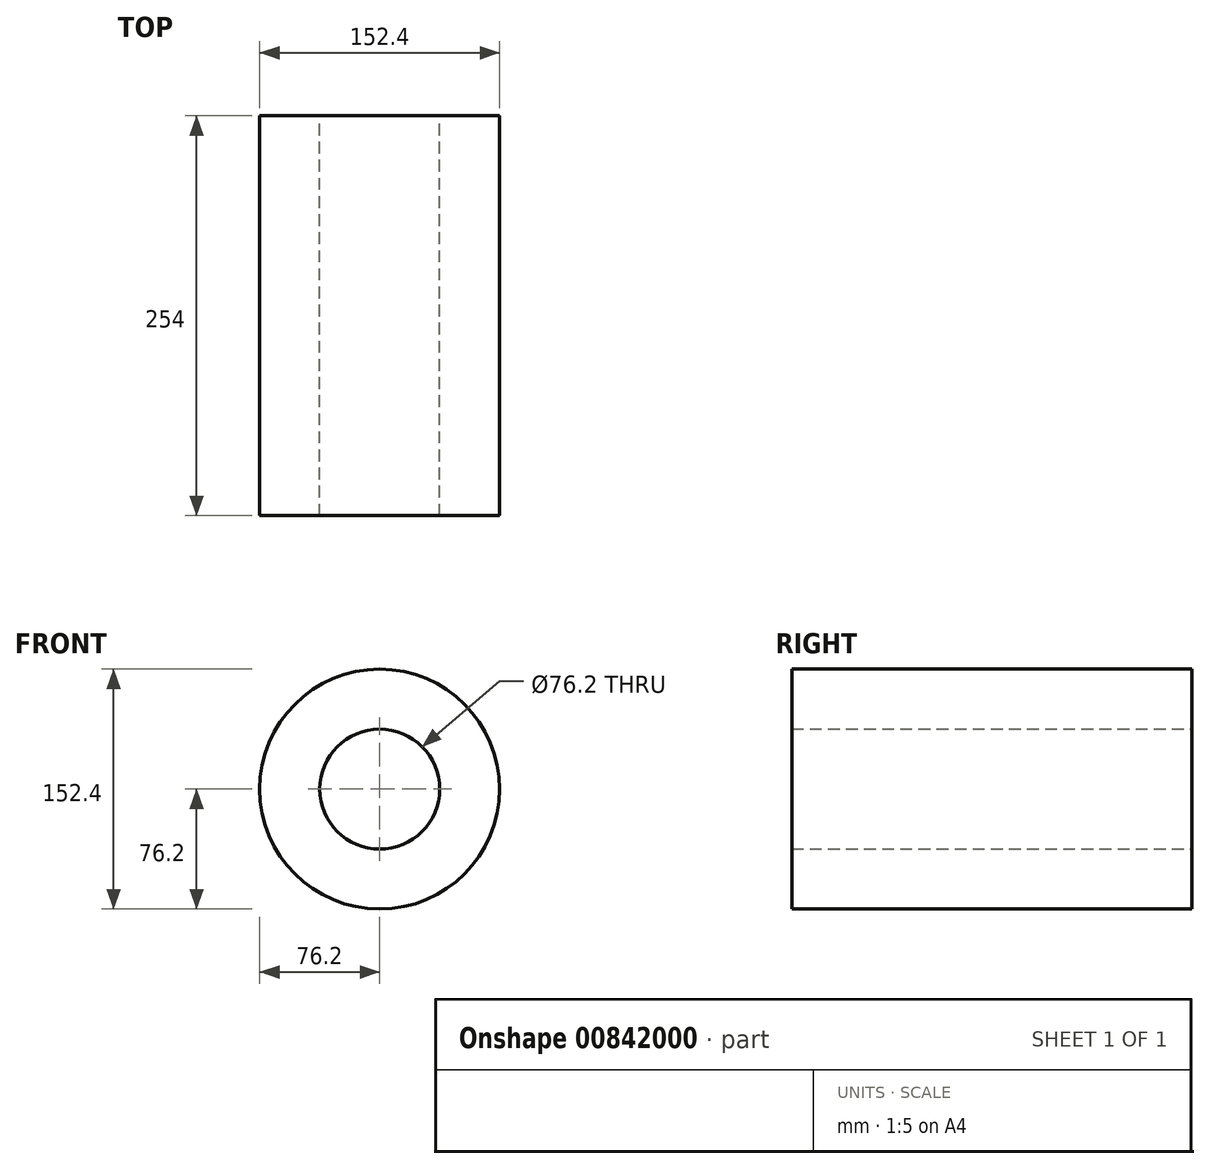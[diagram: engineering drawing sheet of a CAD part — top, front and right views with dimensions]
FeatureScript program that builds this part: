
annotation { "Feature Type Name" : "Feature", "Feature Type Description" : "" }
export const myFeature = defineFeature(function(context is Context, id is Id, definition is map)
    precondition{}
    {
        {
            var Q0;
            Q0=qCreatedBy(makeId("Front.planeOp"),FACE);
            var sketch = newSketch(context, id + "F0", { "sketchPlane" : qUnion([Q0])});
            skCircle(sketch, "E0", {"center": v(0, 0) * mm, "radius": 76.2 * mm});
            skCircle(sketch, "E1", {"center": v(0, 0) * mm, "radius": 38.1 * mm});
            skSolve(sketch);
        }
        {
            var Q0;
            Q0=makeQuery(id+"F0.imprint","IMPRINT",FACE,{"disambiguationData":[TD([[makeQuery(id+"F0.imprint","IMPRINT",EDGE,{"derivedFrom":sQuery(id+"F0.wireOp",EDGE,"E0")}),1.0]])]});
            extrude(context, id + "F1", {"entities" : qUnion([Q0]), "endBound" : BoundingType.SYMMETRIC, "depth" : 254 * mm, "offsetDistance" : 25.4 * mm});
        }
    });
